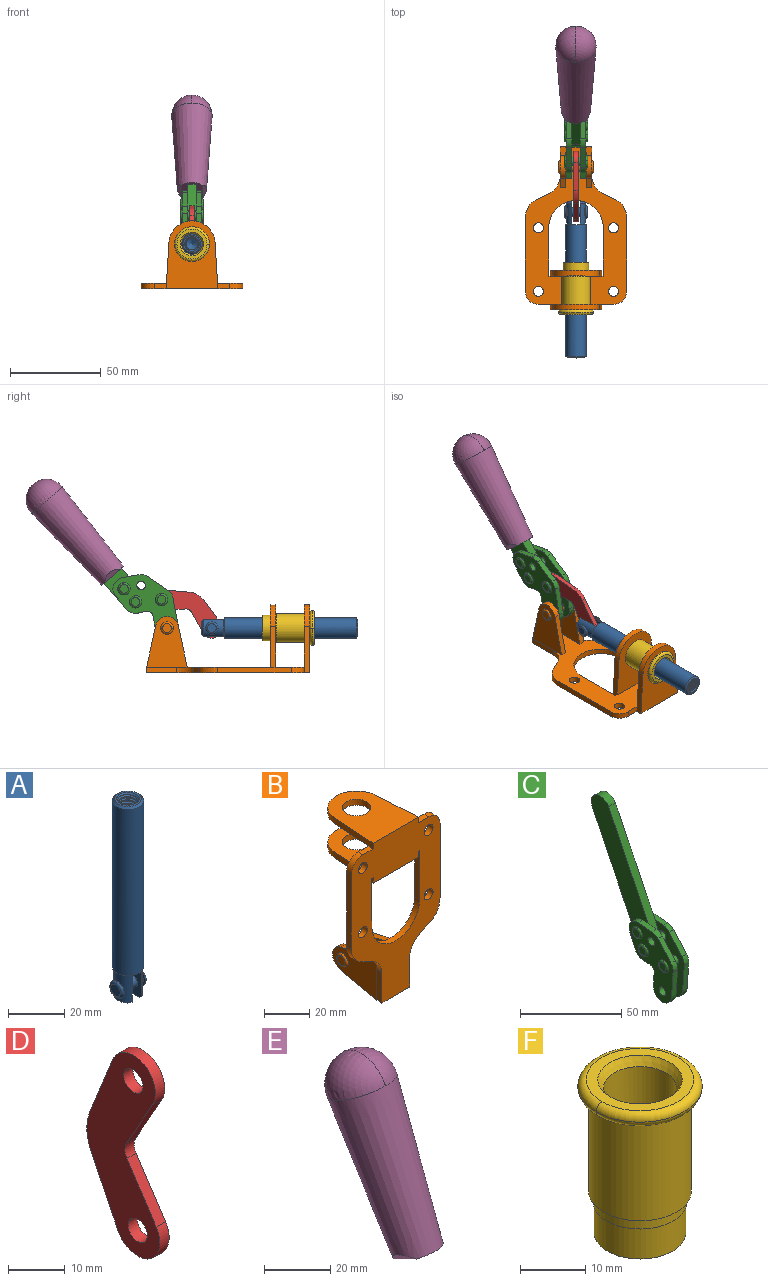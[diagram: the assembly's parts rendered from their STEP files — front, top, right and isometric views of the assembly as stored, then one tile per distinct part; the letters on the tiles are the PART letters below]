
ASSEMBLY  parts=6 mates=6
PART A: 48 faces, bbox 12.6x11.1x86.1 mm
  f0: torus R=2.41mm, axis (-1,0,0), area 15mm2, adj f30,f32,f34
  f1: torus R=2.41mm, axis (-1,0,0), area 15mm2, adj f29,f31,f33
  f2: cylinder r=5.54mm len=72.39mm, axis (0,0,1), area 2518.5mm2, adj f3,f4,f42,f43
  f3: cone r=5.54mm half-angle=45deg, axis (0,0,1), area 7.6mm2, adj f2,f5,f41
  f4: cone r=5.54mm half-angle=45deg, axis (0,0,-1), area 34.9mm2, adj f2,f39
  f5: cylinder r=5.08mm len=11.48mm, axis (0,0,1), area 108.3mm2, adj f3,f7,f8,f41
  f6: cylinder r=2.41mm len=4.83mm, axis (-1,0,0), area 71.2mm2, adj f40,f41
  f7: cylinder r=2.41mm len=4.83mm, axis (-1,0,0), area 7.6mm2, adj f5,f34
  f8: cone r=5.08mm half-angle=45deg, axis (0,0,1), area 10.6mm2, adj f5,f37,f41
  f9: cone r=3.98mm half-angle=45deg, axis (0,0,1), area 17.6mm2, adj f27,f39,f45,f46,f47
  f10: cylinder r=2.41mm len=4.83mm, axis (-1,0,0), area 7.6mm2, adj f33,f38
  f11: cylinder r=3.2mm len=6.4mm, axis (0,0,1), area 78.4mm2, adj f12,f28,f44,f45,f47
  f12: cylinder r=3.2mm len=6.4mm, axis (0,0,1), area 10.5mm2, adj f11,f13,f45,f47
  f13: cylinder r=3.2mm len=6.4mm, axis (0,0,1), area 10.5mm2, adj f12,f14,f45,f47
  f14: cylinder r=3.2mm len=6.4mm, axis (0,0,1), area 10.5mm2, adj f13,f15,f45,f47
  f15: cylinder r=3.2mm len=6.4mm, axis (0,0,1), area 10.5mm2, adj f14,f16,f45,f47
  f16: cylinder r=3.2mm len=6.4mm, axis (0,0,1), area 10.5mm2, adj f15,f17,f45,f47
  f17: cylinder r=3.2mm len=6.4mm, axis (0,0,1), area 10.5mm2, adj f16,f18,f45,f47
  f18: cylinder r=3.2mm len=6.4mm, axis (0,0,1), area 10.5mm2, adj f17,f19,f45,f47
  f19: cylinder r=3.2mm len=6.4mm, axis (0,0,1), area 10.5mm2, adj f18,f20,f45,f47
  f20: cylinder r=3.2mm len=6.4mm, axis (0,0,1), area 10.5mm2, adj f19,f21,f45,f47
  f21: cylinder r=3.2mm len=6.4mm, axis (0,0,1), area 10.5mm2, adj f20,f22,f45,f47
  f22: cylinder r=3.2mm len=6.4mm, axis (0,0,1), area 10.5mm2, adj f21,f23,f45,f47
  f23: cylinder r=3.2mm len=6.4mm, axis (0,0,1), area 10.5mm2, adj f22,f24,f45,f47
  f24: cylinder r=3.2mm len=6.4mm, axis (0,0,1), area 10.5mm2, adj f23,f25,f45,f47
  f25: cylinder r=3.2mm len=6.4mm, axis (0,0,1), area 10.5mm2, adj f24,f26,f45,f47
  f26: cylinder r=3.2mm len=6.4mm, axis (0,0,1), area 10.5mm2, adj f25,f27,f45,f47
  f27: cylinder r=3.2mm len=6.4mm, axis (0,0,1), area 7.4mm2, adj f9,f26,f45,f47
  f28: cone r=3.2mm half-angle=60deg, axis (0,0,1), area 37.2mm2, adj f11
  f29: plane 4.83x4.83mm, normal (-1,0,0), area 18.3mm2, adj f1,f31
  f30: plane 4.83x4.83mm, normal (1,0,0), area 18.3mm2, adj f0,f32
  f31: torus R=2.41mm, axis (-1,0,0), area 15mm2, adj f1,f29,f33
  f32: torus R=2.41mm, axis (-1,0,0), area 15mm2, adj f0,f30,f34
  f33: plane 6.83x6.83mm, normal (1,0,0), area 18.3mm2, adj f1,f10,f31
  f34: plane 6.83x6.83mm, normal (-1,0,0), area 18.3mm2, adj f0,f7,f32
  f35: cone r=5.08mm half-angle=45deg, axis (0,0,1), area 10.6mm2, adj f36,f38,f40
  f36: plane 7.25x1.97mm, normal (0,0,-1), area 10mm2, adj f35,f40
  f37: plane 7.25x1.97mm, normal (0,0,-1), area 10mm2, adj f8,f41
  f38: cylinder r=5.08mm len=11.48mm, axis (0,0,1), area 108.3mm2, adj f10,f35,f40,f42
  f39: plane 9.55x9.55mm, normal (0,0,1), area 22mm2, adj f4,f9
  f40: plane 12.76x10.09mm, normal (1,0,0), area 95.7mm2, adj f6,f35,f36,f38,f42,f43
  f41: plane 12.76x10.09mm, normal (-1,0,0), area 95.7mm2, adj f3,f5,f6,f8,f37,f43
  f42: cone r=5.54mm half-angle=45deg, axis (0,0,1), area 7.6mm2, adj f2,f38,f40
  f43: plane 11.07x4.7mm, normal (0,0,-1), area 50.4mm2, adj f2,f40,f41
  f44: plane 0.89x0.62mm, normal (-1,0,0), area 0.3mm2, adj f11,f45,f46,f47
  f45: bspline ~24.8x7.63mm, area 266.6mm2, adj f9,f11,f12,f13,f14,f15,f16,f17
  f46: bspline ~24.87x7.63mm, area 73.6mm2, adj f9,f44,f45,f47
  f47: bspline ~24.98x7.63mm, area 272.5mm2, adj f9,f11,f12,f13,f14,f15,f16,f17
PART B: 55 faces, bbox 55.7x37.4x89.8 mm
  f0: torus R=2.41mm, axis (-1,0,0), area 15mm2, adj f11,f15,f25
  f1: torus R=2.41mm, axis (-1,0,0), area 15mm2, adj f10,f12,f22
  f2: cylinder r=2.78mm len=5.56mm, axis (0,-1,0), area 54.2mm2, adj f30,f54
  f3: cylinder r=14.99mm len=29.97mm, axis (0,-1,0), area 145.9mm2, adj f30,f49,f53,f54
  f4: cylinder r=2.78mm len=5.56mm, axis (0,-1,0), area 54.2mm2, adj f30,f54
  f5: cylinder r=2.78mm len=5.56mm, axis (0,-1,0), area 54.2mm2, adj f30,f54
  f6: cylinder r=2.78mm len=5.56mm, axis (0,-1,0), area 54.2mm2, adj f30,f54
  f7: cylinder r=6.35mm len=12.7mm, axis (0,0,1), area 123.6mm2, adj f27,f51
  f8: cylinder r=6.35mm len=12.7mm, axis (0,0,-1), area 124.7mm2, adj f21,f35
  f9: cylinder r=2.41mm len=11.18mm, axis (-1,0,0), area 169.4mm2, adj f16,f19
  f10: plane 4.83x4.83mm, normal (1,0,0), area 18.3mm2, adj f1,f12
  f11: plane 4.83x4.83mm, normal (-1,0,0), area 18.3mm2, adj f0,f15
  f12: torus R=2.41mm, axis (-1,0,0), area 15mm2, adj f1,f10,f22
  f13: cylinder r=6.35mm len=12.41mm, axis (1,0,0), area 53.4mm2, adj f18,f19,f22,f23
  f14: cylinder r=6.35mm len=12.41mm, axis (-1,0,0), area 53.4mm2, adj f16,f17,f24,f25
  f15: torus R=2.41mm, axis (-1,0,0), area 15mm2, adj f0,f11,f25
  f16: plane 27.86x22.35mm, normal (1,0,0), area 425.4mm2, adj f9,f14,f17,f24,f30
  f17: plane 22.86x4.97mm, normal (0,0.21,0.98), area 72.5mm2, adj f14,f16,f25,f30
  f18: plane 22.86x4.97mm, normal (0,0.21,0.98), area 72.5mm2, adj f13,f19,f22,f30
  f19: plane 27.86x22.35mm, normal (-1,0,0), area 425.4mm2, adj f9,f13,f18,f23,f30
  f20: cylinder r=12.7mm len=25.35mm, axis (0,0,-1), area 119.8mm2, adj f21,f34,f35,f36
  f21: plane 34.21x28.07mm, normal (0,0,-1), area 702.4mm2, adj f8,f20,f30,f34,f36
  f22: plane 27.96x22.45mm, normal (1,0,0), area 407.2mm2, adj f1,f12,f13,f18,f23,f30,f42,f43
  f23: plane 22.86x4.97mm, normal (0,0.21,-0.98), area 72.5mm2, adj f13,f19,f22,f44
  f24: plane 22.86x4.97mm, normal (0,0.21,-0.98), area 72.5mm2, adj f14,f16,f25,f44
  f25: plane 27.86x22.35mm, normal (-1,0,0), area 407.1mm2, adj f0,f14,f15,f17,f24,f30,f45,f46
  f26: plane 3.1x0.95mm, normal (0,0,-1), area 2.7mm2, adj f30,f49,f50,f54
  f27: plane 34.21x28.07mm, normal (0,0,1), area 702.4mm2, adj f7,f28,f30,f50,f52
  f28: cylinder r=12.7mm len=25.35mm, axis (0,0,1), area 118.8mm2, adj f27,f50,f51,f52
  f29: plane 3.1x0.95mm, normal (0,0,-1), area 2.7mm2, adj f30,f52,f53,f54
  f30: plane 86.54x55.63mm, normal (0,1,0), area 2362.9mm2, adj f2,f3,f4,f5,f6,f16,f17,f18
  f31: plane 40.56x3.1mm, normal (-1,0,0), area 125.7mm2, adj f30,f32,f48,f54
  f32: cylinder r=7.11mm len=7.11mm, axis (0,-1,0), area 34.6mm2, adj f30,f31,f33,f54
  f33: plane 6.67x3.1mm, normal (0,0,1), area 20.4mm2, adj f30,f32,f34,f54
  f34: plane 25.39x3.13mm, normal (-1,0.06,0), area 79.5mm2, adj f20,f21,f33,f35,f54
  f35: plane 37.31x28.45mm, normal (0,0,1), area 789.9mm2, adj f8,f20,f34,f36,f54
  f36: plane 25.39x3.13mm, normal (1,0.06,0), area 79.5mm2, adj f20,f21,f35,f37,f54
  f37: plane 6.67x3.1mm, normal (0,0,1), area 20.4mm2, adj f30,f36,f38,f54
  f38: cylinder r=7.11mm len=7.11mm, axis (0,-1,0), area 34.6mm2, adj f30,f37,f39,f54
  f39: plane 40.56x3.1mm, normal (1,0,0), area 125.7mm2, adj f30,f38,f40,f54
  f40: cylinder r=11.18mm len=10.16mm, axis (0,-1,0), area 39.5mm2, adj f30,f39,f41,f54
  f41: plane 6.09x3.1mm, normal (0.42,0,-0.91), area 20.8mm2, adj f30,f40,f42,f54
  f42: cylinder r=11.18mm len=9.41mm, axis (0,-1,0), area 37.2mm2, adj f22,f30,f41,f43,f54
  f43: plane 16.5x3.1mm, normal (1,0,0), area 51.1mm2, adj f22,f42,f44,f54
  f44: plane 17.37x3.1mm, normal (0,0,-1), area 53.8mm2, adj f23,f24,f30,f43,f45,f54
  f45: plane 16.5x3.1mm, normal (-1,0,0), area 51.1mm2, adj f25,f44,f46,f54
  f46: cylinder r=11.18mm len=9.41mm, axis (0,-1,0), area 37.2mm2, adj f25,f30,f45,f47,f54
  f47: plane 6.09x3.1mm, normal (-0.42,0,-0.91), area 20.8mm2, adj f30,f46,f48,f54
  f48: cylinder r=11.18mm len=10.16mm, axis (0,-1,0), area 39.5mm2, adj f30,f31,f47,f54
  f49: plane 26.54x3.1mm, normal (-1,0,0), area 82.3mm2, adj f3,f26,f30,f54
  f50: plane 25.39x3.1mm, normal (1,0.06,0), area 78.8mm2, adj f26,f27,f28,f51,f54
  f51: plane 37.31x28.45mm, normal (0,0,-1), area 789.9mm2, adj f7,f28,f50,f52,f54
  f52: plane 25.39x3.1mm, normal (-1,0.06,0), area 78.8mm2, adj f27,f28,f29,f51,f54
  f53: plane 26.54x3.1mm, normal (1,0,0), area 82.3mm2, adj f3,f29,f30,f54
  f54: plane 89.66x55.63mm, normal (0,-1,0), area 2678.5mm2, adj f2,f3,f4,f5,f6,f26,f29,f31
PART C: 59 faces, bbox 12.9x60.2x99.6 mm
  f0: torus R=2.39mm, axis (-1,0,0), area 14.9mm2, adj f20,f43,f51
  f1: torus R=2.39mm, axis (-1,0,0), area 14.9mm2, adj f19,f42,f51
  f2: torus R=2.39mm, axis (-1,0,0), area 14.9mm2, adj f18,f35,f51
  f3: torus R=2.39mm, axis (-1,0,0), area 14.9mm2, adj f14,f17,f23
  f4: torus R=2.39mm, axis (-1,0,0), area 14.9mm2, adj f13,f16,f23
  f5: torus R=2.39mm, axis (-1,0,0), area 14.9mm2, adj f12,f15,f23
  f6: cylinder r=2.39mm len=4.78mm, axis (1,0,0), area 46.5mm2, adj f48,f50,f51
  f7: cylinder r=2.39mm len=4.78mm, axis (1,0,0), area 46.5mm2, adj f50,f51
  f8: cylinder r=6.35mm len=12.68mm, axis (1,0,0), area 61.8mm2, adj f38,f39,f50,f51
  f9: cylinder r=2.39mm len=4.78mm, axis (-1,0,0), area 70.5mm2, adj f46,f50
  f10: cylinder r=2.39mm len=4.78mm, axis (-1,0,0), area 46.5mm2, adj f23,f45,f46
  f11: cylinder r=2.39mm len=4.78mm, axis (-1,0,0), area 46.5mm2, adj f23,f46
  f12: plane 4.78x4.78mm, normal (1,0,0), area 17.9mm2, adj f5,f15
  f13: plane 4.78x4.78mm, normal (1,0,0), area 17.9mm2, adj f4,f16
  f14: plane 4.78x4.78mm, normal (1,0,0), area 17.9mm2, adj f3,f17
  f15: torus R=2.39mm, axis (-1,0,0), area 14.9mm2, adj f5,f12,f23
  f16: torus R=2.39mm, axis (-1,0,0), area 14.9mm2, adj f4,f13,f23
  f17: torus R=2.39mm, axis (-1,0,0), area 14.9mm2, adj f3,f14,f23
  f18: plane 4.78x4.78mm, normal (-1,0,0), area 17.9mm2, adj f2,f35
  f19: plane 4.78x4.78mm, normal (-1,0,0), area 17.9mm2, adj f1,f42
  f20: plane 4.78x4.78mm, normal (-1,0,0), area 17.9mm2, adj f0,f43
  f21: plane 2.26x0.2mm, normal (1,0,0), area 0.2mm2, adj f31,f44
  f22: plane 2.26x0.2mm, normal (-1,0,0), area 0.2mm2, adj f41,f44
  f23: plane 39.37x30.77mm, normal (1,0,0), area 565.5mm2, adj f3,f4,f5,f10,f11,f15,f16,f17
  f24: cylinder r=6.1mm len=4.15mm, axis (-1,0,0), area 14.7mm2, adj f23,f25,f32,f46
  f25: plane 10.25x9.01mm, normal (0,-0.75,0.66), area 42.3mm2, adj f23,f24,f26,f46
  f26: cylinder r=6.35mm len=4.64mm, axis (-1,0,0), area 15.6mm2, adj f23,f25,f27,f46
  f27: plane 15.84x3.1mm, normal (0,-1,-0.07), area 49.2mm2, adj f23,f26,f28,f46
  f28: cylinder r=6.35mm len=12.68mm, axis (-1,0,0), area 61.8mm2, adj f23,f27,f29,f46
  f29: plane 8.11x3.1mm, normal (0,1,0.07), area 25.2mm2, adj f23,f28,f30,f46
  f30: cylinder r=3.05mm len=3.25mm, axis (-1,0,0), area 14.8mm2, adj f23,f29,f31,f46
  f31: plane 5.99x3.1mm, normal (0,0.07,-1), area 18.6mm2, adj f21,f23,f30,f44,f46
  f32: plane 9.5x3.1mm, normal (0,-0.07,1), area 29.5mm2, adj f23,f24,f33,f46,f47
  f33: cylinder r=6.1mm len=8.63mm, axis (-1,0,0), area 39.1mm2, adj f23,f32,f34,f47
  f34: plane 8.65x3.96mm, normal (0,0.91,-0.42), area 29.5mm2, adj f23,f33,f44,f47
  f35: torus R=2.39mm, axis (-1,0,0), area 14.9mm2, adj f2,f18,f51
  f36: plane 10.25x9.01mm, normal (0,-0.75,0.66), area 42.3mm2, adj f37,f49,f50,f51
  f37: cylinder r=6.35mm len=4.64mm, axis (1,0,0), area 15.6mm2, adj f36,f38,f50,f51
  f38: plane 15.84x3.1mm, normal (0,-1,-0.07), area 49.2mm2, adj f8,f37,f50,f51
  f39: plane 8.11x3.1mm, normal (0,1,0.07), area 25.2mm2, adj f8,f40,f50,f51
  f40: cylinder r=3.05mm len=3.25mm, axis (1,0,0), area 14.8mm2, adj f39,f41,f50,f51
  f41: plane 5.99x3.1mm, normal (0,0.07,-1), area 18.6mm2, adj f22,f40,f44,f50,f51
  f42: torus R=2.39mm, axis (-1,0,0), area 14.9mm2, adj f1,f19,f51
  f43: torus R=2.39mm, axis (-1,0,0), area 14.9mm2, adj f0,f20,f51
  f44: cylinder r=6.35mm len=12.12mm, axis (-1,0,0), area 128.9mm2, adj f21,f22,f23,f31,f34,f41,f46,f47
  f45: plane 2.65x1.35mm, normal (1,0,0), area 1mm2, adj f10,f55
  f46: plane 39.08x20.42mm, normal (-1,0,0), area 412.5mm2, adj f9,f10,f11,f24,f25,f26,f27,f28
  f47: plane 77.62x39.82mm, normal (1,0,0), area 850mm2, adj f32,f33,f34,f44,f53,f54,f55
  f48: plane 2.65x1.35mm, normal (-1,0,0), area 1mm2, adj f6,f55
  f49: cylinder r=6.1mm len=4.15mm, axis (1,0,0), area 14.7mm2, adj f36,f50,f51,f56
  f50: plane 39.08x20.42mm, normal (1,0,0), area 412.5mm2, adj f6,f7,f8,f9,f36,f37,f38,f39
  f51: plane 39.37x30.77mm, normal (-1,0,0), area 565.5mm2, adj f0,f1,f2,f6,f7,f8,f35,f36
  f52: plane 8.65x3.96mm, normal (0,0.91,-0.42), area 29.5mm2, adj f44,f51,f57,f58
  f53: plane 68.49x33.4mm, normal (0,0.9,-0.44), area 358.1mm2, adj f44,f47,f54,f58
  f54: cylinder r=6.35mm len=12.06mm, axis (1,0,0), area 93.7mm2, adj f47,f53,f55,f58
  f55: plane 68.49x33.4mm, normal (0,-0.9,0.44), area 358.1mm2, adj f44,f45,f46,f47,f48,f50,f54,f58
  f56: plane 9.5x3.1mm, normal (0,-0.07,1), area 29.5mm2, adj f49,f50,f51,f57,f58
  f57: cylinder r=6.1mm len=8.63mm, axis (1,0,0), area 39.1mm2, adj f51,f52,f56,f58
  f58: plane 77.62x39.82mm, normal (-1,0,0), area 850mm2, adj f44,f52,f53,f54,f55,f56,f57
PART D: 12 faces, bbox 2.3x18.2x42.8 mm
  f0: cylinder r=2.4mm len=4.8mm, axis (1,0,0), area 34.9mm2, adj f4,f11
  f1: cylinder r=10.41mm len=8.47mm, axis (1,0,0), area 20.2mm2, adj f4,f9,f10,f11
  f2: cylinder r=3.05mm len=3.16mm, axis (1,0,0), area 7.7mm2, adj f4,f6,f7,f11
  f3: cylinder r=2.4mm len=4.8mm, axis (1,0,0), area 34.9mm2, adj f4,f11
  f4: plane 42.81x18.23mm, normal (-1,0,0), area 414.1mm2, adj f0,f1,f2,f3,f5,f6,f7,f8
  f5: cylinder r=5.54mm len=10.67mm, axis (1,0,0), area 41.8mm2, adj f4,f6,f10,f11
  f6: plane 11.66x6.53mm, normal (0,-0.87,-0.49), area 30.9mm2, adj f2,f4,f5,f11
  f7: plane 11.17x7.33mm, normal (0,-0.84,0.55), area 30.9mm2, adj f2,f4,f8,f11
  f8: cylinder r=5.54mm len=10.51mm, axis (1,0,0), area 41.8mm2, adj f4,f7,f9,f11
  f9: plane 13.67x6.67mm, normal (0,0.9,-0.44), area 35.1mm2, adj f1,f4,f8,f11
  f10: plane 14.1x5.7mm, normal (0,0.93,0.37), area 35.1mm2, adj f1,f4,f5,f11
  f11: plane 42.81x18.23mm, normal (1,0,0), area 414.1mm2, adj f0,f1,f2,f3,f5,f6,f7,f8
PART E: 11 faces, bbox 22.3x42.6x64.5 mm
  f0: sphere r=11.13mm, area 411.4mm2, adj f1,f8
  f1: cone r=11.11mm half-angle=3.3deg, axis (0,0.44,0.9), area 3251.8mm2, adj f0,f7,f8,f9,f10
  f2: cylinder r=6.16mm len=11.7mm, axis (1,0,0), area 89.5mm2, adj f3,f4,f5,f6
  f3: plane 60.23x36.75mm, normal (-1,0,0), area 763.6mm2, adj f2,f4,f6,f10
  f4: plane 51.37x25.05mm, normal (0,0.9,-0.44), area 264.2mm2, adj f2,f3,f5,f10
  f5: plane 60.23x36.75mm, normal (1,0,0), area 763.6mm2, adj f2,f4,f6,f10
  f6: plane 51.37x25.05mm, normal (0,-0.9,0.44), area 264.2mm2, adj f2,f3,f5,f10
  f7: plane 9.95x5.95mm, normal (0.71,-0.31,-0.64), area 25.8mm2, adj f1,f10
  f8: sphere r=11.13mm, area 411.4mm2, adj f0,f1
  f9: plane 9.95x5.95mm, normal (-0.71,-0.31,-0.64), area 25.8mm2, adj f1,f10
  f10: plane 14.27x11.38mm, normal (0,-0.44,-0.9), area 106.7mm2, adj f1,f3,f4,f5,f6,f7,f9
PART F: 15 faces, bbox 20.6x20.6x28.7 mm
  f0: torus R=8.26mm, axis (0,0,1), area 56.8mm2, adj f1,f10,f12
  f1: torus R=8.26mm, axis (0,0,1), area 56.8mm2, adj f0,f6,f13
  f2: cylinder r=5.59mm len=25.91mm, axis (0,0,1), area 909.6mm2, adj f3,f4
  f3: cone r=6.86mm half-angle=45deg, axis (0,0,-1), area 70.2mm2, adj f2,f14
  f4: cone r=6.47mm half-angle=30deg, axis (0,0,1), area 66.7mm2, adj f2,f13
  f5: cylinder r=7.04mm len=14.07mm, axis (0,0,1), area 252.6mm2, adj f11,f14
  f6: torus R=8.26mm, axis (0,0,1), area 56.8mm2, adj f1,f12,f13
  f7: cylinder r=7.16mm len=14.33mm, axis (0,0,1), area 91.5mm2, adj f9,f11
  f8: cylinder r=7.86mm len=18.42mm, axis (0,0,1), area 909.6mm2, adj f9,f10
  f9: plane 15.72x15.72mm, normal (0,0,-1), area 33mm2, adj f7,f8
  f10: plane 16.51x16.51mm, normal (0,0,-1), area 19.9mm2, adj f0,f8,f12
  f11: plane 14.33x14.33mm, normal (0,0,-1), area 5.7mm2, adj f5,f7
  f12: torus R=8.26mm, axis (0,0,1), area 56.8mm2, adj f0,f6,f10
  f13: plane 16.51x16.51mm, normal (0,0,1), area 82.7mm2, adj f1,f4,f6
  f14: plane 14.07x14.07mm, normal (0,0,-1), area 7.8mm2, adj f3,f5
PLACE A rot(axis=(1,0,0),90deg) t=(0,24.17,-3.1)mm
PLACE B rot(axis=(1,0,0),90deg) t=(0,1.23,-3.1)mm fixed
PLACE C rot(axis=(-1,0,0),15deg) t=(0,17.86,58.88)mm
PLACE D rot(axis=(1,0,0),121.4deg) t=(0,34.72,8.56)mm
PLACE E rot(axis=(-1,0,0),15deg) t=(-0.04,17.86,58.88)mm
PLACE F rot(axis=(1,0,0),90deg) t=(0,1.23,-3.1)mm
MATE revolute D.f3 <-> C.f4  axis (1,0,0) through (0,36.35,37.1)mm
MATE fastened E.f2 <-> C.f54  axis (1,0,0) through (-2.35,100.65,93.4)mm
MATE slider A.f2 <-> B.f7  axis (0,-1,0) through (0,-34.62,21.51)mm
MATE revolute C.f7 <-> B.f0  axis (1,0,0) through (0,33.32,21.51)mm
MATE fastened F.f2 <-> B.f7  axis (0,1,0) through (0,-45.16,21.51)mm
MATE revolute D.f5 <-> A.f6  axis (1,0,0) through (0,8.69,21.51)mm
